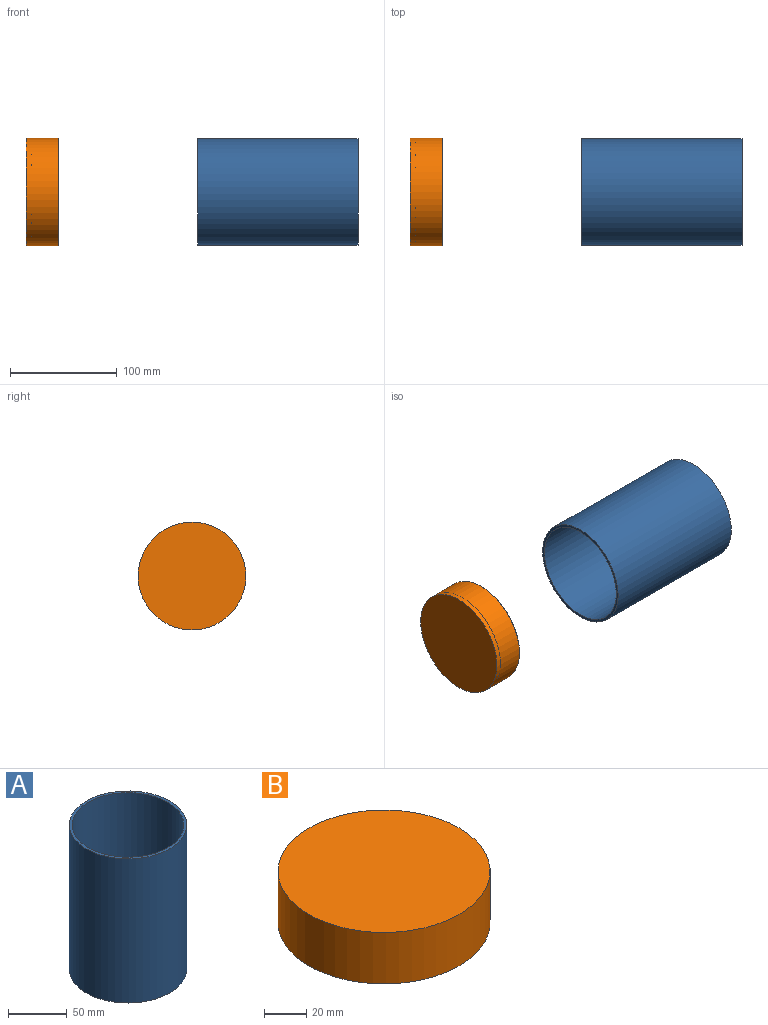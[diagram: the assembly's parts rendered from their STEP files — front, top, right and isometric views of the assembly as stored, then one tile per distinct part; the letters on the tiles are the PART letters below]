
ASSEMBLY  parts=2 mates=1
PART A: 7 faces, bbox 100x100x150 mm
  f0: cylinder r=50mm len=150mm, axis (0,0,-1), area 47123.9mm2, adj f1,f2
  f1: plane 100x100mm, normal (0,0,1), area 765.8mm2, adj f0,f3
  f2: plane 100x100mm, normal (0,0,-1), area 765.8mm2, adj f0,f5
  f3: cylinder r=47.5mm len=140mm, axis (0,0,1), area 41783.2mm2, adj f1,f4
  f4: plane 95x95mm, normal (0,0,1), area 7088.2mm2, adj f3
  f5: cylinder r=47.5mm len=95mm, axis (0,0,-1), area 1492.3mm2, adj f2,f6
  f6: plane 95x95mm, normal (0,0,-1), area 7088.2mm2, adj f5
PART B: 5 faces, bbox 101x101x30 mm
  f0: cylinder r=50.5mm len=101mm, axis (0,0,-1), area 9519mm2, adj f1,f2
  f1: plane 101x101mm, normal (0,0,1), area 8011.8mm2, adj f0
  f2: plane 101x101mm, normal (0,0,-1), area 157.9mm2, adj f0,f3
  f3: cylinder r=50mm len=100mm, axis (0,0,-1), area 7854mm2, adj f2,f4
  f4: plane 100x100mm, normal (0,0,-1), area 7854mm2, adj f3
PLACE A rot(axis=(0,-1,0),90deg) t=(246.18,123.59,349.25)mm
PLACE B rot(axis=(0,-1,0),90deg) t=(-34.95,123.59,349.25)mm
MATE slider B.f0 <-> A.f0  axis (1,0,0) through (-59.95,123.59,349.25)mm
